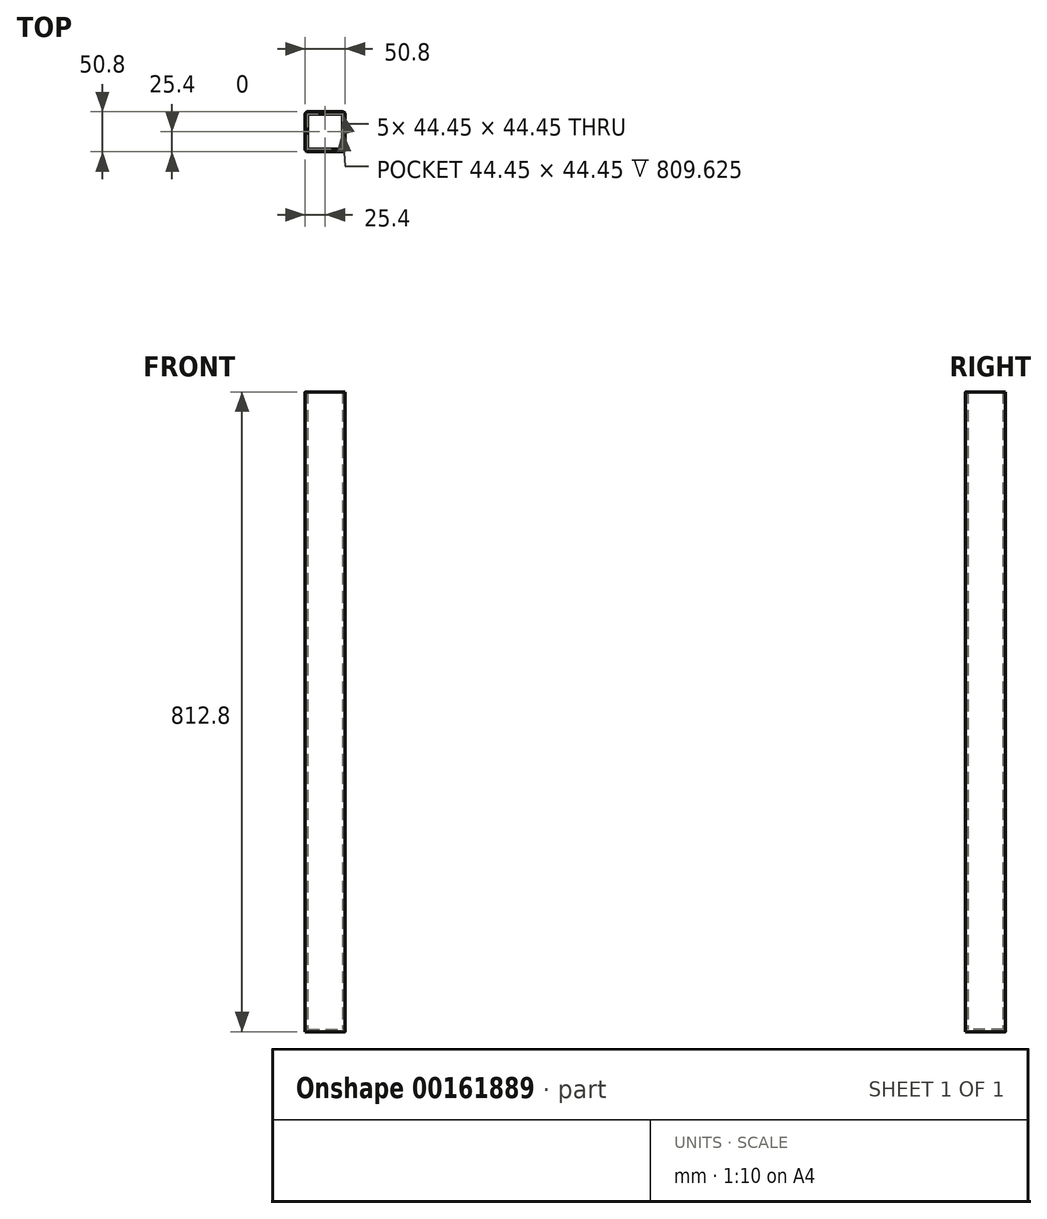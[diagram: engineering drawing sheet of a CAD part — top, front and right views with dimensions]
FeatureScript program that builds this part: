
annotation { "Feature Type Name" : "Feature", "Feature Type Description" : "" }
export const myFeature = defineFeature(function(context is Context, id is Id, definition is map)
    precondition{}
    {
        {
            var Q0;
            Q0=qCreatedBy(makeId("Top.planeOp"),FACE);
            var sketch = newSketch(context, id + "F0", { "sketchPlane" : qUnion([Q0])});
            skLineSegment(sketch, "E0.bottom", {"start": v(-22.23, 25.4) * mm, "end": v(22.23, 25.4) * mm});
            skLineSegment(sketch, "E0.top", {"start": v(-22.23, -25.4) * mm, "end": v(22.23, -25.4) * mm});
            skLineSegment(sketch, "E0.left", {"start": v(-25.4, 22.23) * mm, "end": v(-25.4, -22.23) * mm});
            skLineSegment(sketch, "E0.right", {"start": v(25.4, 22.23) * mm, "end": v(25.4, -22.23) * mm});
            skPoint(sketch, "E0.middle", {"position": v(0, 0) * mm});
            skPoint(sketch, "E1.visualSharp", {"position": v(-25.4, 25.4) * mm});
            skArc(sketch, "E1.filletArc", {"start": v(-22.23, 25.4) * mm, "mid": v(-24.47, 24.47) * mm, "end": v(-25.4, 22.23) * mm});
            skPoint(sketch, "E2.visualSharp", {"position": v(-25.4, -25.4) * mm});
            skArc(sketch, "E2.filletArc", {"start": v(-25.4, -22.23) * mm, "mid": v(-24.47, -24.47) * mm, "end": v(-22.23, -25.4) * mm});
            skPoint(sketch, "E3.visualSharp", {"position": v(25.4, -25.4) * mm});
            skArc(sketch, "E3.filletArc", {"start": v(22.23, -25.4) * mm, "mid": v(24.47, -24.47) * mm, "end": v(25.4, -22.23) * mm});
            skPoint(sketch, "E4.visualSharp", {"position": v(25.4, 25.4) * mm});
            skArc(sketch, "E4.filletArc", {"start": v(25.4, 22.23) * mm, "mid": v(24.47, 24.47) * mm, "end": v(22.23, 25.4) * mm});
            skSolve(sketch);
        }
        {
            var Q0;
            Q0 = qSketchRegion(id + "F0", true);
            extrude(context, id + "F1", {"entities" : qUnion([Q0]), "depth" : 812.8 * mm});
        }
        {
            var Q0;
            Q0=makeQuery(id+"F1.opExtrude","CAP_FACE",FACE,{"disambiguationData":[OSD([sQuery(id+"F0.wireOp",EDGE,"E0.bottom"),sQuery(id+"F0.wireOp",EDGE,"E0.top"),sQuery(id+"F0.wireOp",EDGE,"E0.left"),sQuery(id+"F0.wireOp",EDGE,"E0.right"),sQuery(id+"F0.wireOp",EDGE,"E1.filletArc"),sQuery(id+"F0.wireOp",EDGE,"E2.filletArc"),sQuery(id+"F0.wireOp",EDGE,"E3.filletArc"),sQuery(id+"F0.wireOp",EDGE,"E4.filletArc")])],"isStart":false});
            shell(context, id + "F2", {"entities" : qUnion([Q0]), "thickness" : 3.17 * mm});
        }
    });
